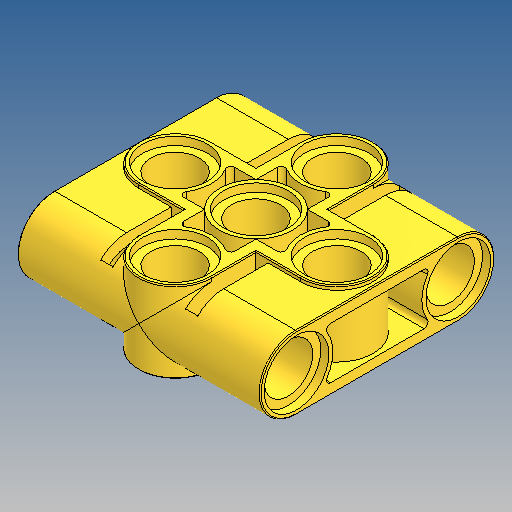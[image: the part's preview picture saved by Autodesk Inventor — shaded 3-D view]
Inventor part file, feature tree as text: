
AUTODESK INVENTOR PART (.ipt)
format: ipt  version: 2025 (Build 290162010, 162A)  size: 587,264 bytes
history: native  units: in
note: dims shown in document units (in); Inventor stores cm internally (conversion verified against a paired STEP export)
features: extrude x8, sketch x3, mirror x1, fillet x1
ambient origin geometry x8: Origin, YZ Plane, XZ Plane, XY Plane, X Axis, Y Axis, Z Axis, Center Point
bodies: Solid1 (feature_tree)
feature tree (13):
  extrude  "Extrusion1"  Depth=0.2835in
  sketch  "Sketch3"  dims[d4=45.0deg d5=0.9449in]
  extrude  "Extrusion3"  Depth=0.9449in
  extrude  "Extrusion2"  Depth=0.2835in
  extrude  "Extrusion4"  Depth=0.189in
  extrude  "Extrusion5"  Depth=0.252in
  extrude  "Extrusion8"  Depth=0.315in
  sketch  "Sketch4"  dims[d6=0.0in d7=0.2835in d8=0.189in d9=0.252in d10=0.315in d11=0.0in d12=0.315in d13=0.0in d14=0.0472in d15=0.1002in d16=0.315in d17=0.0in d18=0.252in d19=0.0in d20=0.189in d21=0.252in d22=0.315in d23=0.0in d24=0.0315in d25=0.0in d26=0.063in d27=0.0in d28=0.0039in d29=0.0157in]
  extrude  "Extrusion6"  TaperAngle=0.0deg  [1 undecoded]
  extrude  "Extrusion7"  Depth=0.315in TaperAngle=0.0deg
  mirror  "Mirror1"
  fillet  "Fillet1"  Radius=0.0472in
  sketch  "Sketch2"  dims[d2=0.6299in d3=0.2835in]
note: 1 required parameter value undecoded (feature->parameter linkage not recoverable at this tier; creation-order binding heuristic only, values carry confidence <= 0.55)
